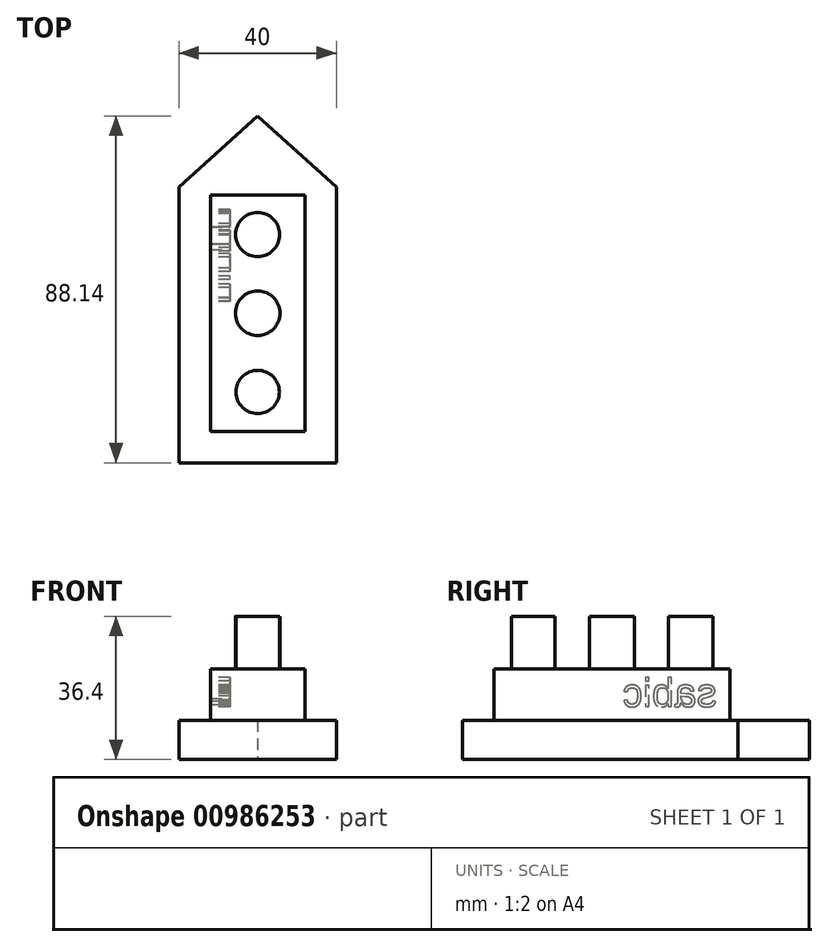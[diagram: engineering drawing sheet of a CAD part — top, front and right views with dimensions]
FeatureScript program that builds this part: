
annotation { "Feature Type Name" : "Feature", "Feature Type Description" : "" }
export const myFeature = defineFeature(function(context is Context, id is Id, definition is map)
    precondition{}
    {
        {
            var Q0;
            Q0=qCreatedBy(makeId("Top.planeOp"),FACE);
            var sketch = newSketch(context, id + "F0", { "sketchPlane" : qUnion([Q0])});
            skLineSegment(sketch, "E0", {"start": v(-20, 37.78) * mm, "end": v(-20, -32.22) * mm});
            skLineSegment(sketch, "E1", {"start": v(-20, -32.22) * mm, "end": v(20, -32.22) * mm});
            skLineSegment(sketch, "E2", {"start": v(20, -32.22) * mm, "end": v(20, 37.78) * mm});
            skLineSegment(sketch, "E3", {"start": v(-20, 37.78) * mm, "end": v(0, 55.92) * mm});
            skLineSegment(sketch, "E4", {"start": v(0, 55.92) * mm, "end": v(20, 37.78) * mm});
            skSolve(sketch);
        }
        {
            var Q0;
            Q0=makeQuery(id+"F0.imprint","IMPRINT",FACE,{"disambiguationData":[TD([[makeQuery(id+"F0.imprint","IMPRINT",EDGE,{"derivedFrom":sQuery(id+"F0.wireOp",EDGE,"E0")}),1.0]])]});
            extrude(context, id + "F1", {"entities" : qUnion([Q0]), "depth" : 10 * mm, "offsetDistance" : 25 * mm});
        }
        {
            var Q0;
            Q0=makeQuery(id+"F1.opExtrude","CAP_FACE",FACE,{"disambiguationData":[OSD([sQuery(id+"F0.wireOp",EDGE,"E0"),sQuery(id+"F0.wireOp",EDGE,"E1"),sQuery(id+"F0.wireOp",EDGE,"E2"),sQuery(id+"F0.wireOp",EDGE,"E3"),sQuery(id+"F0.wireOp",EDGE,"E4")])],"isStart":false});
            var sketch = newSketch(context, id + "F2", { "sketchPlane" : qUnion([Q0])});
            skLineSegment(sketch, "E5", {"start": v(-12, 35.78) * mm, "end": v(-12, -24.22) * mm});
            skLineSegment(sketch, "E6", {"start": v(-12, 35.78) * mm, "end": v(12, 35.78) * mm});
            skLineSegment(sketch, "E7", {"start": v(12, 35.78) * mm, "end": v(12, -24.22) * mm});
            skLineSegment(sketch, "E8", {"start": v(-12, -24.22) * mm, "end": v(12, -24.22) * mm});
            skSolve(sketch);
        }
        {
            var Q0;
            Q0=makeQuery(id+"F2.imprint","IMPRINT",FACE,{"disambiguationData":[TD([[makeQuery(id+"F2.imprint","IMPRINT",EDGE,{"derivedFrom":sQuery(id+"F2.wireOp",EDGE,"E5")}),1.0]])]});
            extrude(context, id + "F3", {"entities" : qUnion([Q0]), "operationType" : NewBodyOperationType.ADD, "depth" : 13 * mm, "offsetDistance" : 25 * mm});
        }
        {
            var Q0;
            Q0=makeQuery(id+"F3.opExtrude","CAP_FACE",FACE,{"disambiguationData":[OSD([sQuery(id+"F2.wireOp",EDGE,"E5"),sQuery(id+"F2.wireOp",EDGE,"E6"),sQuery(id+"F2.wireOp",EDGE,"E7"),sQuery(id+"F2.wireOp",EDGE,"E8")])],"isStart":false});
            var sketch = newSketch(context, id + "F4", { "sketchPlane" : qUnion([Q0])});
            skCircle(sketch, "E9", {"center": v(0, 25.78) * mm, "radius": 5.6 * mm});
            skCircle(sketch, "E10", {"center": v(0, 5.78) * mm, "radius": 5.67 * mm});
            skCircle(sketch, "E11", {"center": v(0, -14.22) * mm, "radius": 5.5 * mm});
            skSolve(sketch);
        }
        {
            var Q0;
            Q0=makeQuery(id+"F4.imprint","IMPRINT",FACE,{"disambiguationData":[TD([[makeQuery(id+"F4.imprint","IMPRINT",EDGE,{"derivedFrom":sQuery(id+"F4.wireOp",EDGE,"E9")}),1.0]])]});
            var Q1;
            Q1=makeQuery(id+"F4.imprint","IMPRINT",FACE,{"disambiguationData":[TD([[makeQuery(id+"F4.imprint","IMPRINT",EDGE,{"derivedFrom":sQuery(id+"F4.wireOp",EDGE,"E10")}),1.0]])]});
            var Q2;
            Q2=makeQuery(id+"F4.imprint","IMPRINT",FACE,{"disambiguationData":[TD([[makeQuery(id+"F4.imprint","IMPRINT",EDGE,{"derivedFrom":sQuery(id+"F4.wireOp",EDGE,"E11")}),1.0]])]});
            extrude(context, id + "F5", {"entities" : qUnion([Q0, Q1, Q2]), "operationType" : NewBodyOperationType.ADD, "depth" : 13.4 * mm, "offsetDistance" : 25 * mm});
        }
        {
            var Q0;
            Q0=makeQuery(id+"F3.opExtrude","SWEPT_FACE",FACE,{"disambiguationData":[OSD([sQuery(id+"F2.wireOp",EDGE,"E5")])]});
            var sketch = newSketch(context, id + "F6", { "sketchPlane" : qUnion([Q0])});
            skText(sketch, "E12", { "text": "sabic", "fontName": "Arimo-Regular.ttf"});
            const initialGuessF6  = {"E12": [-0.03243, 0.01346, 1, 0, 0.00737]};
            skSetInitialGuess(sketch, initialGuessF6);
            skSolve(sketch);
        }
        {
            var Q0;
            Q0 = qSketchRegion(id + "F6", true);
            extrude(context, id + "F7", {"entities" : qUnion([Q0]), "operationType" : NewBodyOperationType.REMOVE, "oppositeDirection" : true, "depth" : 5 * mm, "offsetDistance" : 25 * mm});
        }
    });
